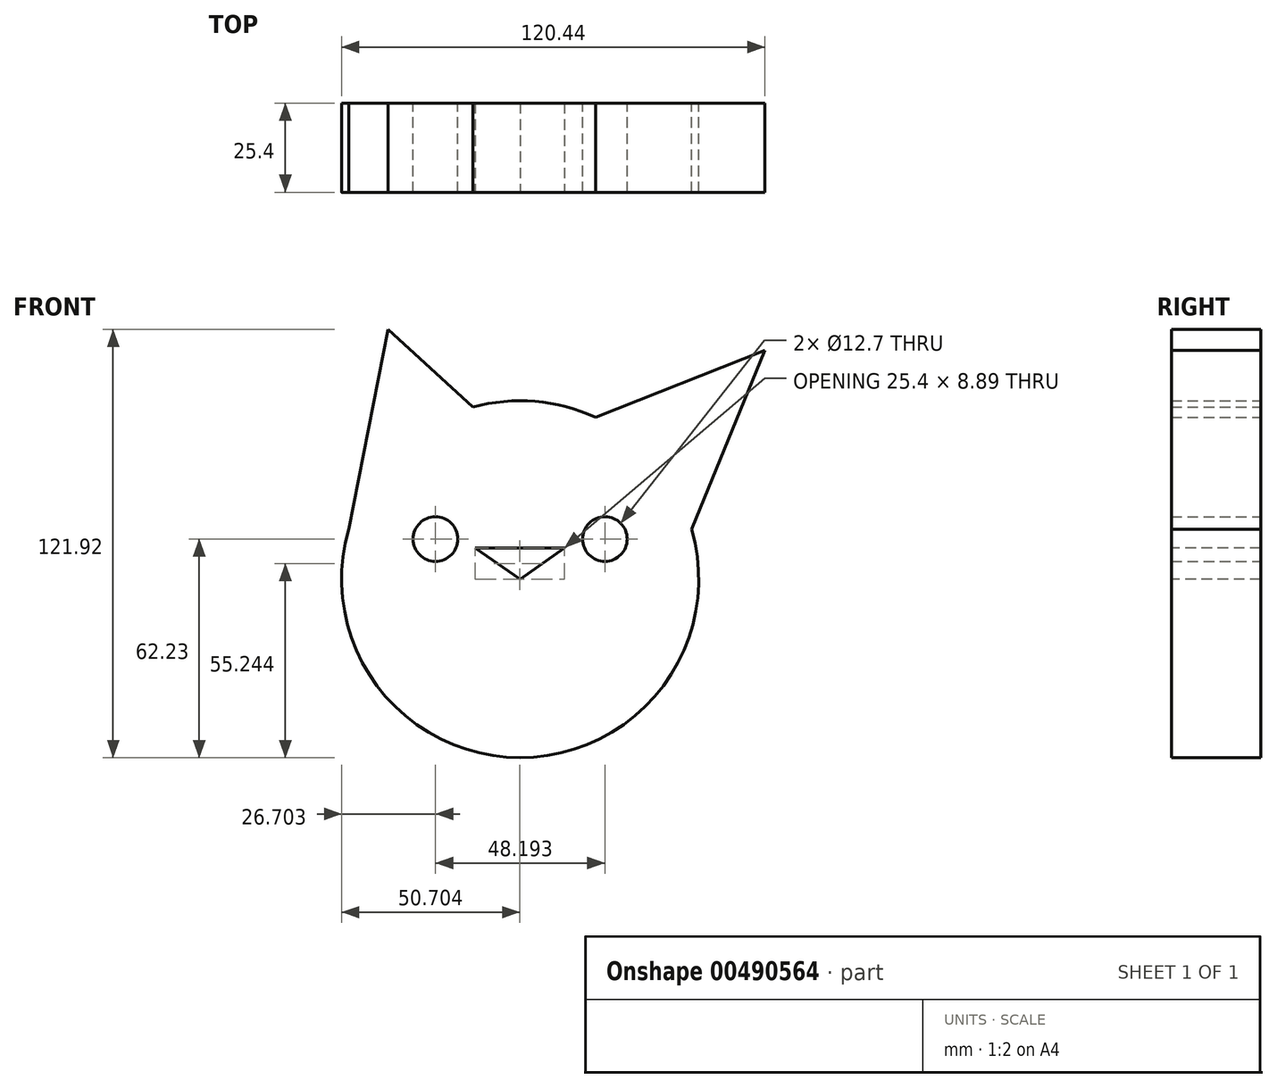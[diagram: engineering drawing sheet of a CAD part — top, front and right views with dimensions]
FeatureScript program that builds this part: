
annotation { "Feature Type Name" : "Feature", "Feature Type Description" : "" }
export const myFeature = defineFeature(function(context is Context, id is Id, definition is map)
    precondition{}
    {
        {
            var Q0;
            Q0=qCreatedBy(makeId("Front.planeOp"),FACE);
            var sketch = newSketch(context, id + "F0", { "sketchPlane" : qUnion([Q0])});
            skArc(sketch, "E0", {"start": v(-48.76, 14.23) * mm, "mid": v(0, -50.8) * mm, "end": v(48.76, 14.23) * mm});
            skCircle(sketch, "E1", {"center": v(-24.1, 11.43) * mm, "radius": 6.35 * mm});
            skCircle(sketch, "E2", {"center": v(24.1, 11.43) * mm, "radius": 6.35 * mm});
            skLineSegment(sketch, "E3", {"start": v(-48.76, 14.23) * mm, "end": v(-37.58, 71.12) * mm});
            skLineSegment(sketch, "E4", {"start": v(-37.58, 71.12) * mm, "end": v(-13.49, 48.98) * mm});
            skLineSegment(sketch, "E5", {"start": v(48.76, 14.23) * mm, "end": v(69.64, 65.2) * mm});
            skLineSegment(sketch, "E6", {"start": v(69.64, 65.2) * mm, "end": v(21.4, 46.07) * mm});
            skArc(sketch, "E7.trimOffspring", {"start": v(21.4, 46.07) * mm, "mid": v(4.22, 50.62) * mm, "end": v(-13.49, 48.98) * mm});
            skSolve(sketch);
        }
        {
            var Q0;
            Q0=makeQuery(id+"F0.imprint","IMPRINT",FACE,{"disambiguationData":[TD([[makeQuery(id+"F0.imprint","IMPRINT",EDGE,{"derivedFrom":sQuery(id+"F0.wireOp",EDGE,"E0")}),1.0]])]});
            extrude(context, id + "F1", {"entities" : qUnion([Q0]), "depth" : 25.4 * mm});
        }
        {
            var Q0;
            Q0=makeQuery(id+"F1.opExtrude","CAP_FACE",FACE,{"disambiguationData":[OSD([sQuery(id+"F0.wireOp",EDGE,"E0"),sQuery(id+"F0.wireOp",EDGE,"E1"),sQuery(id+"F0.wireOp",EDGE,"E2")])],"isStart":false});
            var sketch = newSketch(context, id + "F2", { "sketchPlane" : qUnion([Q0])});
            skLineSegment(sketch, "E8", {"start": v(-12.8, 8.89) * mm, "end": v(12.6, 8.89) * mm});
            skLineSegment(sketch, "E9", {"start": v(12.6, 8.89) * mm, "end": v(0, 0) * mm});
            skLineSegment(sketch, "E10", {"start": v(0, 0) * mm, "end": v(-12.8, 8.89) * mm});
            skSolve(sketch);
        }
        {
            var Q0;
            Q0=makeQuery(id+"F2.imprint","IMPRINT",FACE,{"disambiguationData":[TD([[makeQuery(id+"F2.imprint","IMPRINT",EDGE,{"derivedFrom":sQuery(id+"F2.wireOp",EDGE,"E8")}),-1.0]])]});
            extrude(context, id + "F3", {"entities" : qUnion([Q0]), "operationType" : NewBodyOperationType.REMOVE, "endBound" : BoundingType.THROUGH_ALL, "oppositeDirection" : true, "depth" : 25.4 * mm});
        }
    });
